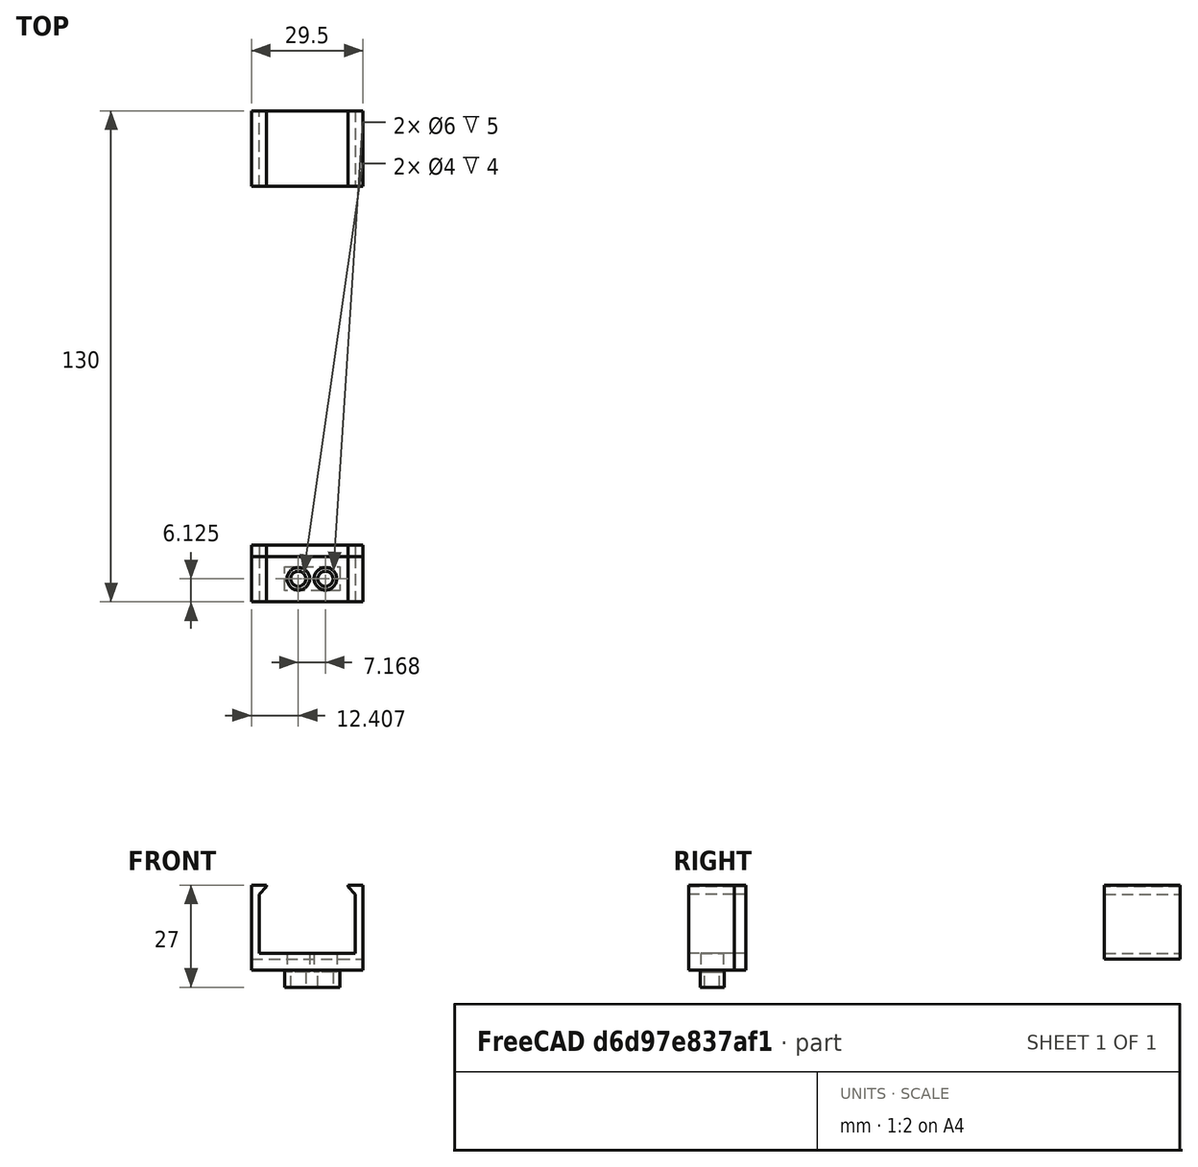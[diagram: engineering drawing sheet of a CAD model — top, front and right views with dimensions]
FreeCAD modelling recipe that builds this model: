
FCSTD DOCUMENT  (FreeCAD 1.1R20251125 (Git shallow))
Label: 9VBatteryClipModel
License: All rights reserved
LicenseURL: https://en.wikipedia.org/wiki/All_rights_reserved
objects: Sketcher::SketchObject×4, PartDesign::Pad×3, Part::FeaturePython×3, Part::Feature×2, PartDesign::Pocket×2, Mesh::Feature×1, Part::Refine×1, App::Point×1, PartDesign::SubShapeBinder×1, PartDesign::Plane×1, PartDesign::Body×1, App::DocumentObjectGroup×1
note: 32 computed .brp shape members not serialized (recipe doc carries the construction recipe); baked Part::Feature solids carry a one-line shape summary decoded from their .brp

FEATURE [Mesh::Feature] _9vClip_plain  label="9vClip_plain"
FEATURE [Part::Feature] _9vClip_plain001
  shape: bbox 29.5 x 20 x 19.5 mm, 52 faces, 0 solids (baked)
FEATURE [Part::Feature] _9vClip_plain001_solid  label="_9vClip_plain001 (Solid)"
  shape: bbox 29.5 x 20 x 19.5 mm, 52 faces (baked)
FEATURE [Part::Refine] _9vClip_plain001_solid001  label="_9vClip_plain001 (Solid)001"
  Source = -> _9vClip_plain001_solid
FEATURE [App::Point] Origin001
  Role = Origin
FEATURE [PartDesign::SubShapeBinder] Binder
  BindCopyOnChange = 0
  BindMode = 0
  ClaimChildren = false
  Context = -> Body [Binder.]
  Fuse = false
  MakeFace = true
  OffsetFill = false
  OffsetIntersection = false
  OffsetJoinType = 0
  OffsetOpenResult = false
  PartialLoad = false
  Refine = true
  Relative = true
  Support = -> [_9vClip_plain001_solid001]
  _Version = 2
FEATURE [Sketcher::SketchObject] Sketch
  ArcFitTolerance = 1e-06
  AttachmentSupport = -> [Origin]
  ExternalGeometry = -> [Binder]
  ExternalTypes = [0,0,0,0,0,0,0,0,0,0,0,0]
  FullyConstrained = true
  MakeInternals = false
  MapMode = 5
  Placement = pos=(0,0,0) rot=(1,0,0;1.5708rad)
  sketch-geometry (13):
    g0: LineSegment StartX=-115.8 StartY=19.5 StartZ=0 EndX=-117.8 EndY=19.5 EndZ=0
    g1: LineSegment StartX=-117.8 StartY=19.5 StartZ=0 EndX=-119.8 EndY=19.5 EndZ=0
    g2: LineSegment StartX=-119.8 StartY=19.5 StartZ=0 EndX=-119.8 EndY=0 EndZ=0
    g3: LineSegment StartX=-119.8 StartY=0 StartZ=0 EndX=-90.3 EndY=0 EndZ=0
    g4: LineSegment StartX=-90.3 StartY=0 StartZ=0 EndX=-90.3 EndY=19.5 EndZ=0
    g5: LineSegment StartX=-90.3 StartY=19.5 StartZ=0 EndX=-94.3 EndY=19.5 EndZ=0
    g6: LineSegment StartX=-94.3 StartY=19.5 StartZ=0 EndX=-94.3 EndY=19.1 EndZ=0
    g7: LineSegment StartX=-94.3 StartY=19.1 StartZ=0 EndX=-92.3 EndY=17.1 EndZ=0
    g8: LineSegment StartX=-92.3 StartY=17.1 StartZ=0 EndX=-92.3 EndY=1.5 EndZ=0
    g9: LineSegment StartX=-92.3 StartY=1.5 StartZ=0 EndX=-117.8 EndY=1.5 EndZ=0
    g10: LineSegment StartX=-117.8 StartY=1.5 StartZ=0 EndX=-117.8 EndY=17.1 EndZ=0
    g11: LineSegment StartX=-117.8 StartY=17.1 StartZ=0 EndX=-115.8 EndY=19.1 EndZ=0
    g12: LineSegment StartX=-115.8 StartY=19.1 StartZ=0 EndX=-115.8 EndY=19.5 EndZ=0
  constraints (26):
    c: Coincident(g-4,g0)
    c: Coincident(g0,g-14)
    c: Coincident(g0,g1)
    c: Coincident(g1,g-6)
    c: Coincident(g1,g2)
    c: Coincident(g2,g-7)
    c: Coincident(g2,g3)
    c: Coincident(g3,g-8)
    c: Coincident(g3,g4)
    c: Coincident(g4,g-9)
    c: Coincident(g4,g5)
    c: Coincident(g5,g-10)
    c: Coincident(g5,g6)
    c: Coincident(g6,g-11)
    c: Coincident(g6,g7)
    c: Coincident(g7,g-12)
    c: Coincident(g7,g8)
    c: Coincident(g8,g-13)
    c: Coincident(g8,g9)
    c: Coincident(g9,g-14)
    c: Coincident(g9,g10)
    c: Coincident(g10,g-3)
    c: Coincident(g10,g11)
    c: Coincident(g11,g-3)
    c: Coincident(g11,g12)
    c: Coincident(g12,g0)
FEATURE [PartDesign::Pad] Pad
  Direction = (0,-1,2e-16)
  Length = 15
  Length2 = 10
  Profile = -> Sketch
  ReferenceAxis = -> Sketch [N_Axis]
  Refine = true
  SideType = 0
  Suppressed = false
  Type = 0
  Type2 = 0
FEATURE [Sketcher::SketchObject] Sketch001
  ArcFitTolerance = 1e-06
  AttachmentSupport = -> [Pad]
  ExternalGeometry = -> [Pad]
  ExternalTypes = [0,0,0,0]
  FullyConstrained = true
  MakeInternals = false
  MapMode = 5
  Placement = pos=(0,0,0) rot=(1,0,0;3.14159rad)
  sketch-geometry (4):
    g0: LineSegment StartX=-119.8 StartY=15 StartZ=0 EndX=-119.8 EndY=0 EndZ=0
    g1: LineSegment StartX=-119.8 StartY=0 StartZ=0 EndX=-90.3 EndY=0 EndZ=0
    g2: LineSegment StartX=-90.3 StartY=0 StartZ=0 EndX=-90.3 EndY=15 EndZ=0
    g3: LineSegment StartX=-90.3 StartY=15 StartZ=0 EndX=-119.8 EndY=15 EndZ=0
  constraints (10):
    c: Coincident(g0,g1)
    c: Coincident(g1,g2)
    c: Coincident(g2,g3)
    c: Coincident(g3,g0)
    c: Vertical(g0)
    c: Vertical(g2)
    c: Horizontal(g1)
    c: Horizontal(g3)
    c: Coincident(g0,g-4)
    c: Coincident(g1,g-6)
FEATURE [PartDesign::Pad] Pad001
  BaseFeature = -> Pad
  Direction = (0,0,-1)
  Length = 3
  Length2 = 10
  Profile = -> Sketch001
  ReferenceAxis = -> Sketch001 [N_Axis]
  Refine = true
  SideType = 0
  Suppressed = false
  Type = 0
  Type2 = 0
FEATURE [Sketcher::SketchObject] Sketch002
  ArcFitTolerance = 1e-06
  AttachmentSupport = -> [Pad001]
  ExternalGeometry = -> [Pad001]
  ExternalTypes = [0,0,0,0]
  FullyConstrained = false
  MakeInternals = false
  MapMode = 5
  Placement = pos=(0,0,-3) rot=(1,0,0;3.14159rad)
  sketch-geometry (12):
    g0: LineSegment [constr] StartX=-90.3 StartY=15 StartZ=0 EndX=-96.41 EndY=15 EndZ=0
    g1: LineSegment [constr] StartX=-96.41 StartY=15 StartZ=0 EndX=-96.4153 EndY=12.05 EndZ=0
    g2: LineSegment StartX=-96.4153 StartY=12.05 StartZ=0 EndX=-111.015 EndY=12.05 EndZ=0
    g3: LineSegment StartX=-111.015 StartY=12.05 StartZ=0 EndX=-111.015 EndY=5.71 EndZ=0
    g4: LineSegment StartX=-111.015 StartY=5.71 StartZ=0 EndX=-96.4153 EndY=5.71 EndZ=0
    g5: LineSegment StartX=-96.4153 StartY=5.71 StartZ=0 EndX=-96.4153 EndY=12.05 EndZ=0
    g6: LineSegment [constr] StartX=-100.225 StartY=12.05 StartZ=0 EndX=-96.4153 EndY=12.05 EndZ=0
    g7: LineSegment [constr] StartX=-100.225 StartY=8.875 StartZ=0 EndX=-100.225 EndY=12.05 EndZ=0
    g8: LineSegment [constr] StartX=-107.393 StartY=12.05 StartZ=0 EndX=-96.4153 EndY=12.05 EndZ=0
    g9: LineSegment [constr] StartX=-107.393 StartY=8.875 StartZ=0 EndX=-107.393 EndY=12.05 EndZ=0
    g10: Circle CenterX=-107.393 CenterY=8.875 CenterZ=0 NormalX=0 NormalY=0 NormalZ=1 AngleXU=0 Radius=2
    g11: Circle CenterX=-100.225 CenterY=8.875 CenterZ=0 NormalX=0 NormalY=0 NormalZ=1 AngleXU=0 Radius=2
  constraints (31):
    c: Distance(g0) = 6.11
    c: Horizontal(g0)
    c: Coincident(g0,g-5)
    c: Distance(g1) = 2.95
    c: Angle(g-1,g1) = -1.57259
    c: Coincident(g1,g0)
    c: Coincident(g2,g3)
    c: Coincident(g3,g4)
    c: Coincident(g4,g5)
    c: Coincident(g5,g2)
    c: Horizontal(g2)
    c: Horizontal(g4)
    c: Vertical(g3)
    c: Vertical(g5)
    c: Distance(g3,g5) = 14.6
    c: Distance(g2,g4) = 6.34
    c: Coincident(g2,g1)
    c: Distance(g6) = 3.81
    c: Horizontal(g6)
    c: Coincident(g6,g1)
    c: Distance(g7) = 3.175
    c: Angle(g-1,g7) = 1.5708
    c: Coincident(g7,g6)
    c: Distance(g8) = 10.978
    c: Horizontal(g8)
    c: Coincident(g8,g1)
    c: Distance(g9) = 3.175
    c: Angle(g-1,g9) = 1.5708
    c: Coincident(g9,g8)
    c: Diameter(g10) = 4
    c: Diameter(g11) = 4
FEATURE [PartDesign::Pad] Pad002
  BaseFeature = -> Pad001
  Direction = (0,0,-1)
  Length = 4.5
  Length2 = 10
  Profile = -> Sketch002
  ReferenceAxis = -> Sketch002 [N_Axis]
  Refine = true
  SideType = 0
  Suppressed = false
  Type = 0
  Type2 = 0
FEATURE [Sketcher::SketchObject] Sketch003
  ArcFitTolerance = 1e-06
  AttachmentSupport = -> [Pad002]
  ExternalGeometry = -> [Pad002]
  ExternalTypes = [0,0]
  FullyConstrained = true
  MakeInternals = false
  MapMode = 5
  Placement = pos=(0,0,-3) rot=(1,0,0;3.14159rad)
  sketch-geometry (2):
    g0: Circle CenterX=-107.393 CenterY=8.875 CenterZ=0 NormalX=0 NormalY=0 NormalZ=1 AngleXU=0 Radius=3
    g1: Circle CenterX=-100.225 CenterY=8.875 CenterZ=0 NormalX=0 NormalY=0 NormalZ=1 AngleXU=0 Radius=3
  constraints (4):
    c: Diameter(g0) = 6
    c: Coincident(g0,g-3)
    c: Diameter(g1) = 6
    c: Coincident(g1,g-4)
FEATURE [PartDesign::Pocket] Pocket
  BaseFeature = -> Pad002
  Direction = (0,0,1)
  Length = 5
  Length2 = 5
  Profile = -> Sketch003
  ReferenceAxis = -> Sketch003 [N_Axis]
  Refine = true
  SideType = 0
  Suppressed = false
  Type = 0
  Type2 = 0
FEATURE [PartDesign::Plane] DatumPlane
  AttachmentOffset = pos=(0,0,-3) rot=(0,0,1;0rad)
  AttachmentSupport = -> [Pad002]
  Length = 161.818
  MapMode = 5
  Placement = pos=(0,-3,7e-16) rot=(0,0.707107,0.707107;3.14159rad)
  ResizeMode = 0
  Width = 67.0176
FEATURE [PartDesign::Pocket] Pocket001
  BaseFeature = -> Pocket
  Direction = (0,0,1)
  Length = -0.5
  Length2 = 5
  Profile = -> Sketch003
  ReferenceAxis = -> Sketch003 [N_Axis]
  Refine = true
  SideType = 0
  Suppressed = false
  Type = 0
  Type2 = 0
FEATURE [PartDesign::Body] Body
  AllowCompound = false
  Group = -> [Binder,Sketch,Pad,Sketch001,Pad001,Sketch002,Pad002,Sketch003,Pocket,DatumPlane,Pocket001]
  Origin = -> Origin
  Tip = -> Pocket001
FEATURE [Part::FeaturePython] Slice  # WARN: FeaturePython — macro-defined, semantics opaque (R4)
  Base = -> Body
  Mode = 1
  Tolerance = 0
  Tools = -> [DatumPlane]
FEATURE [Part::FeaturePython] Slice_child0  label="Slice.0"  # WARN: FeaturePython — macro-defined, semantics opaque (R4)
  Base = -> Slice
  FilterType = 1
  Invert = false
  OverrideMaxVal = 0
  WindowFrom = 80
  WindowTo = 100
  items = 0
FEATURE [Part::FeaturePython] Slice_child1  label="Slice.1"  # WARN: FeaturePython — macro-defined, semantics opaque (R4)
  Base = -> Slice
  FilterType = 1
  Invert = false
  OverrideMaxVal = 0
  WindowFrom = 80
  WindowTo = 100
  items = 1
FEATURE [App::DocumentObjectGroup] GrExplode_Slice  label="Exploded Slice"
  Group = -> [Slice_child0,Slice_child1]
